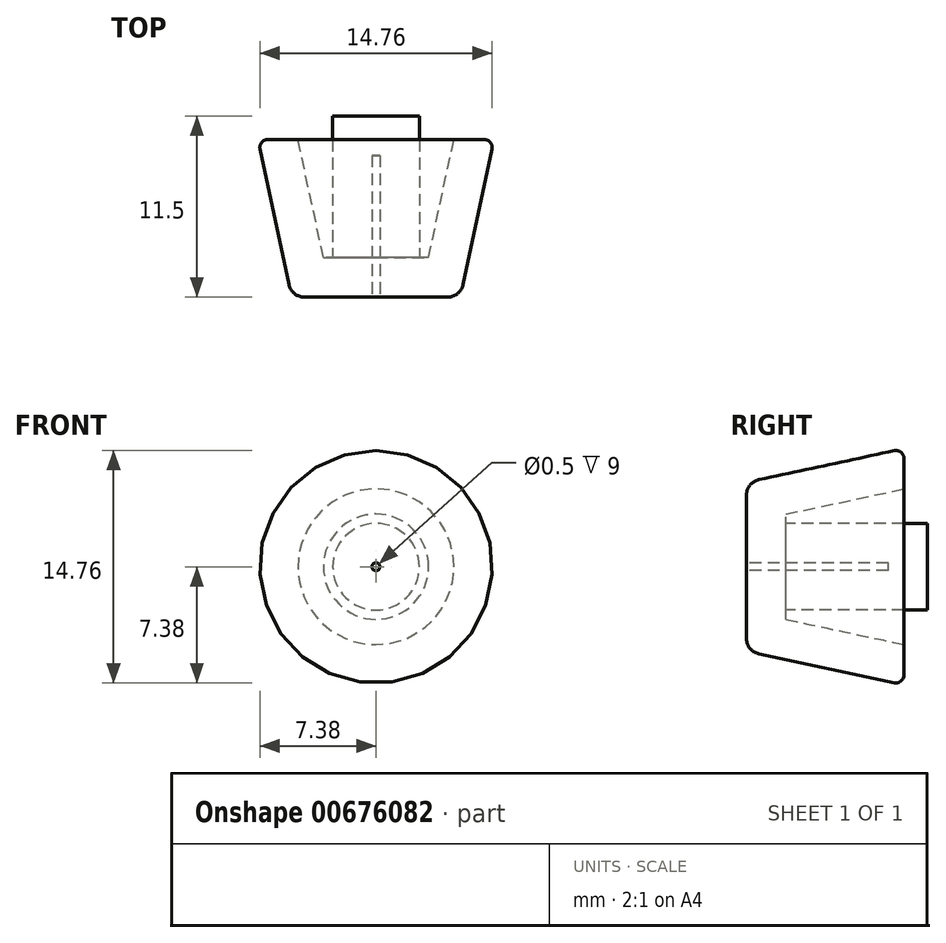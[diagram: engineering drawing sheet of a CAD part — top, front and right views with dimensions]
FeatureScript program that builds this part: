
annotation { "Feature Type Name" : "Feature", "Feature Type Description" : "" }
export const myFeature = defineFeature(function(context is Context, id is Id, definition is map)
    precondition{}
    {
        {
            var Q0;
            Q0=qCreatedBy(makeId("Right.planeOp"),FACE);
            var sketch = newSketch(context, id + "F0", { "sketchPlane" : qUnion([Q0])});
            skLineSegment(sketch, "E0.top", {"start": v(5, -3.75) * mm, "end": v(-5, -3.75) * mm});
            skLineSegment(sketch, "E0.left", {"start": v(5, 3.13) * mm, "end": v(5, -3.75) * mm});
            skLineSegment(sketch, "E0.right", {"start": v(-5, 0.8) * mm, "end": v(-5, -3.75) * mm});
            skPoint(sketch, "E0.middle", {"position": v(0, 0) * mm});
            skLineSegment(sketch, "E1", {"start": v(4.4, 3.62) * mm, "end": v(-4.2, 1.78) * mm});
            skPoint(sketch, "E2.visualSharp", {"position": v(-5, 1.61) * mm});
            skArc(sketch, "E2.filletArc", {"start": v(-4.2, 1.78) * mm, "mid": v(-4.78, 1.43) * mm, "end": v(-5, 0.8) * mm});
            skPoint(sketch, "E3.visualSharp", {"position": v(5, 3.75) * mm});
            skArc(sketch, "E3.filletArc", {"start": v(5, 3.13) * mm, "mid": v(4.81, 3.52) * mm, "end": v(4.4, 3.62) * mm});
            skSolve(sketch);
        }
        {
            var Q0;
            Q0=makeQuery(id+"F0.imprint","IMPRINT",FACE,{"disambiguationData":[TD([[makeQuery(id+"F0.imprint","IMPRINT",EDGE,{"derivedFrom":sQuery(id+"F0.wireOp",EDGE,"E0.top")}),-1.0]])]});
            var Q1;
            Q1=sQuery(id+"F0.wireOp",EDGE,"E0.top");
            revolve(context, id + "F1", {"entities" : qUnion([Q0]), "axis" : qUnion([Q1]), "revolveType" : RevolveType.FULL});
        }
        {
            var Q0;
            Q0=makeQuery(id+"F1.opRevolve","SWEPT_FACE",FACE,{"disambiguationData":[OSD([sQuery(id+"F0.wireOp",EDGE,"E0.right")])]});
            var sketch = newSketch(context, id + "F2", { "sketchPlane" : qUnion([Q0])});
            skCircle(sketch, "E4", {"center": v(0, -3.75) * mm, "radius": 0.25 * mm});
            skSolve(sketch);
        }
        {
            var Q0;
            Q0=makeQuery(id+"F2.imprint","IMPRINT",FACE,{"disambiguationData":[TD([[makeQuery(id+"F2.imprint","IMPRINT",EDGE,{"derivedFrom":sQuery(id+"F2.wireOp",EDGE,"E4")}),1.0]])]});
            var Q1;
            Q1=sQuery(id+"F2.wireOp",EDGE,"E4");
            extrude(context, id + "F3", {"entities" : qUnion([Q0]), "operationType" : NewBodyOperationType.REMOVE, "surfaceEntities" : qUnion([Q1]), "oppositeDirection" : true, "depth" : 9 * mm, "offsetDistance" : 25 * mm});
        }
        {
            var Q0;
            Q0=makeQuery(id+"F1.opRevolve","SWEPT_FACE",FACE,{"disambiguationData":[OSD([sQuery(id+"F0.wireOp",EDGE,"E0.left")])]});
            shell(context, id + "F4", {"entities" : qUnion([Q0]), "thickness" : 2.5 * mm});
        }
    });
